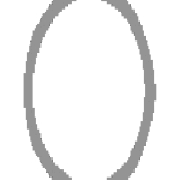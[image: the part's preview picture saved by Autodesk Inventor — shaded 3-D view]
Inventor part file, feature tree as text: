
AUTODESK INVENTOR PART (.ipt)
format: ipt  version: 2021 (Build 250183000, 183)  size: 110,592 bytes
history: native  units: in
note: dims shown in document units (in); Inventor stores cm internally (conversion verified against a paired STEP export)
features: other x4, sketch x3, plane x1
ambient origin geometry x8: Origin, YZ Plane, XZ Plane, XY Plane, X Axis, Y Axis, Z Axis, Center Point
bodies: Solid1 (feature_tree), Body (feature_tree)
feature tree (8):
  other  "Driven Length"
  other  "Frame Generator"
  other  "Start Plane"
  other  "End Plane"
  sketch  "Sketch"  dims[d2=11.6851in d4=-0.0in d5=11.6851in d6=0.12in d7=0.0in d8=90.0deg d9=11.6851in]
  sketch  "Sketch2"  dims[d0=1.0in]
  plane  "Work Plane3"
  sketch  "Sketch3"  dims[d1=0.065in]
